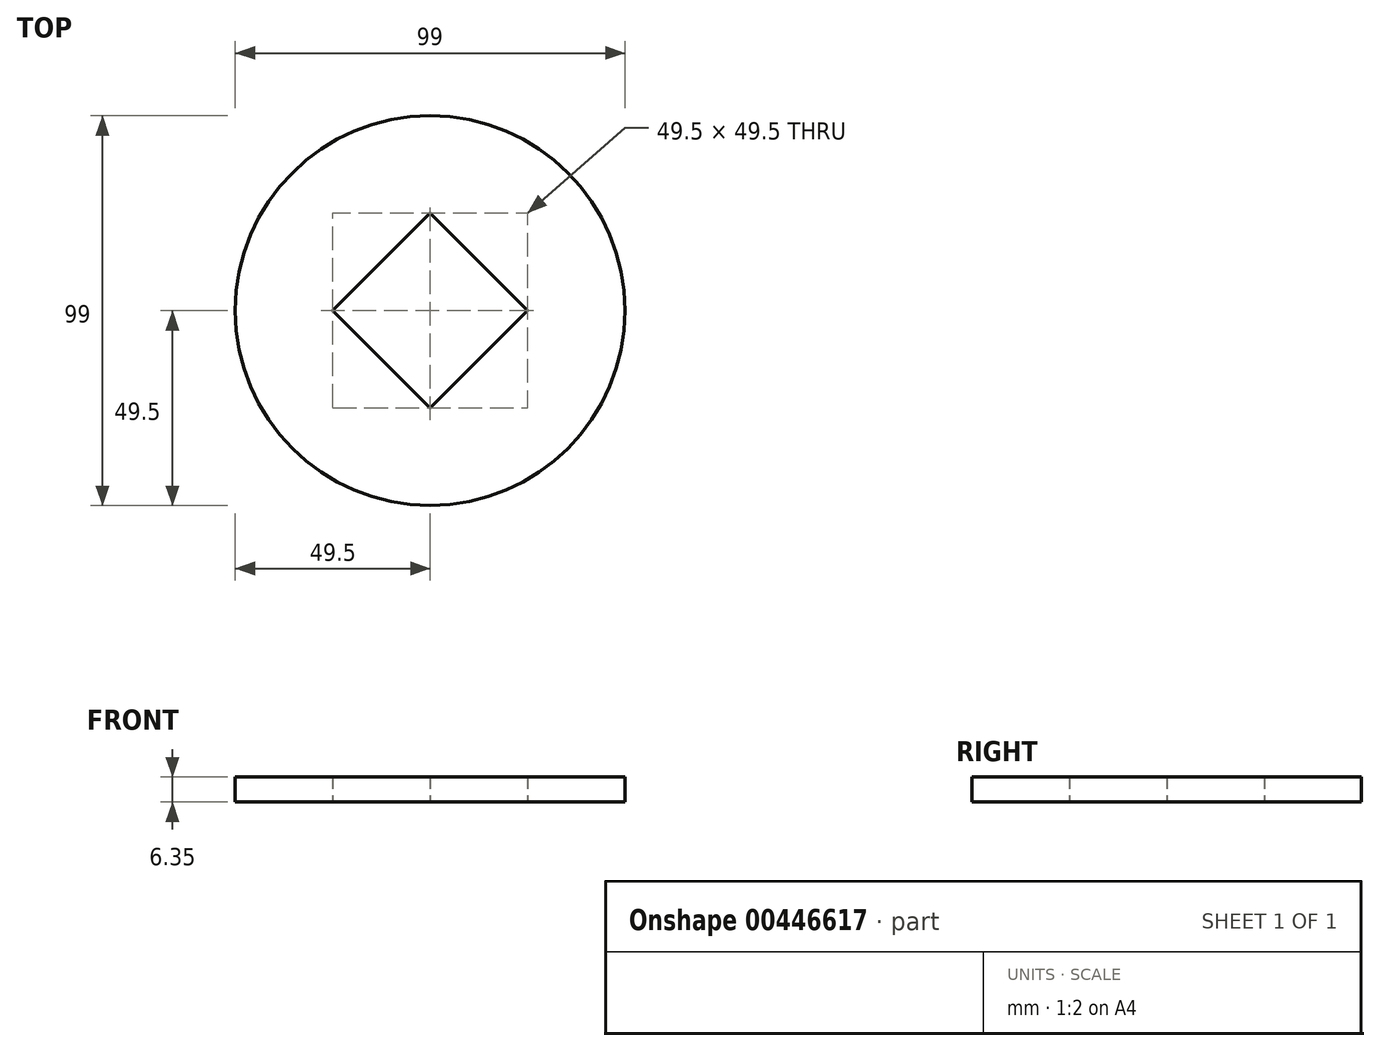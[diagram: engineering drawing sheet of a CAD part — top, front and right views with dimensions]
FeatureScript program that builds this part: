
annotation { "Feature Type Name" : "Feature", "Feature Type Description" : "" }
export const myFeature = defineFeature(function(context is Context, id is Id, definition is map)
    precondition{}
    {
        {
            var Q0;
            Q0=qCreatedBy(makeId("Top.planeOp"),FACE);
            var sketch = newSketch(context, id + "F0", { "sketchPlane" : qUnion([Q0])});
            skCircle(sketch, "E0", {"center": v(0, 0) * mm, "radius": 49.5 * mm});
            skLineSegment(sketch, "E1", {"start": v(0, 24.75) * mm, "end": v(0, 0) * mm, "construction": true});
            skLineSegment(sketch, "E2", {"start": v(24.75, 0) * mm, "end": v(0, 0) * mm, "construction": true});
            skLineSegment(sketch, "E3", {"start": v(0, 0) * mm, "end": v(0, -24.75) * mm, "construction": true});
            skLineSegment(sketch, "E4", {"start": v(0, -24.75) * mm, "end": v(0, 0) * mm, "construction": true});
            skLineSegment(sketch, "E5", {"start": v(-24.75, 0) * mm, "end": v(0, 0) * mm, "construction": true});
            skLineSegment(sketch, "E6", {"start": v(0, 24.75) * mm, "end": v(-24.75, 0) * mm});
            skLineSegment(sketch, "E7", {"start": v(-24.75, 0) * mm, "end": v(0, -24.75) * mm});
            skLineSegment(sketch, "E8", {"start": v(0, -24.75) * mm, "end": v(24.75, 0) * mm});
            skLineSegment(sketch, "E9", {"start": v(24.75, 0) * mm, "end": v(0, 24.75) * mm});
            skSolve(sketch);
        }
        {
            var Q0;
            Q0 = qSketchRegion(id + "F0", true);
            extrude(context, id + "F1", {"entities" : qUnion([Q0]), "depth" : 6.35 * mm});
        }
    });
